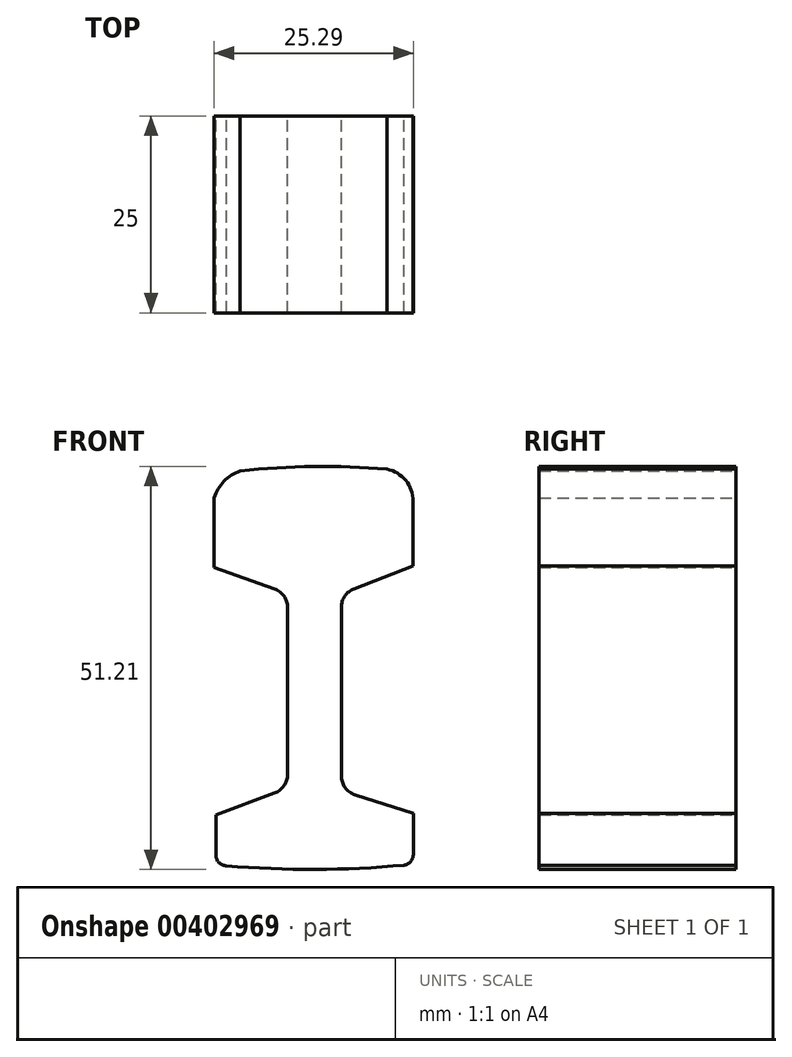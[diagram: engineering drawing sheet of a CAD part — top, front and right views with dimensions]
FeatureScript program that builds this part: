
annotation { "Feature Type Name" : "Feature", "Feature Type Description" : "" }
export const myFeature = defineFeature(function(context is Context, id is Id, definition is map)
    precondition{}
    {
        {
            var Q0;
            Q0=qCreatedBy(makeId("Front.planeOp"),FACE);
            var sketch = newSketch(context, id + "F0", { "sketchPlane" : qUnion([Q0])});
            skLineSegment(sketch, "E0", {"start": v(-32.08, 49.25) * mm, "end": v(-32.08, 28.1) * mm});
            skLineSegment(sketch, "E1", {"start": v(-25.28, 49.3) * mm, "end": v(-25.28, 27.9) * mm});
            skLineSegment(sketch, "E2", {"start": v(-23.64, 51.66) * mm, "end": v(-16.14, 54.54) * mm});
            skLineSegment(sketch, "E3", {"start": v(-33.77, 51.64) * mm, "end": v(-41.42, 54.38) * mm});
            skLineSegment(sketch, "E4", {"start": v(-33.73, 25.71) * mm, "end": v(-41.19, 22.92) * mm});
            skLineSegment(sketch, "E5", {"start": v(-23.51, 25.49) * mm, "end": v(-16.13, 23.13) * mm});
            skPoint(sketch, "E6.visualSharp", {"position": v(-32.08, 26.33) * mm});
            skArc(sketch, "E6.filletArc", {"start": v(-33.73, 25.71) * mm, "mid": v(-32.53, 26.65) * mm, "end": v(-32.08, 28.1) * mm});
            skPoint(sketch, "E7.visualSharp", {"position": v(-25.28, 26.05) * mm});
            skArc(sketch, "E7.filletArc", {"start": v(-25.28, 27.9) * mm, "mid": v(-24.79, 26.41) * mm, "end": v(-23.51, 25.49) * mm});
            skPoint(sketch, "E8.visualSharp", {"position": v(-25.28, 51.04) * mm});
            skArc(sketch, "E8.filletArc", {"start": v(-23.64, 51.66) * mm, "mid": v(-24.83, 50.73) * mm, "end": v(-25.28, 49.3) * mm});
            skPoint(sketch, "E9.visualSharp", {"position": v(-32.08, 51.04) * mm});
            skArc(sketch, "E9.filletArc", {"start": v(-32.08, 49.25) * mm, "mid": v(-32.55, 50.71) * mm, "end": v(-33.77, 51.64) * mm});
            skLineSegment(sketch, "E10", {"start": v(-16.13, 23.13) * mm, "end": v(-16.13, 17.86) * mm});
            skLineSegment(sketch, "E11", {"start": v(-41.19, 22.92) * mm, "end": v(-41.19, 17.8) * mm});
            skArc(sketch, "E12", {"start": v(-39.86, 16.47) * mm, "mid": v(-28.58, 16) * mm, "end": v(-17.3, 16.55) * mm});
            skArc(sketch, "E13", {"start": v(-41.19, 17.8) * mm, "mid": v(-40.8, 16.86) * mm, "end": v(-39.86, 16.47) * mm});
            skArc(sketch, "E14", {"start": v(-17.3, 16.55) * mm, "mid": v(-16.47, 16.98) * mm, "end": v(-16.13, 17.86) * mm});
            skLineSegment(sketch, "E15", {"start": v(-41.42, 54.38) * mm, "end": v(-41.42, 63.21) * mm});
            skLineSegment(sketch, "E16", {"start": v(-16.14, 54.54) * mm, "end": v(-16.14, 62.78) * mm});
            skArc(sketch, "E17", {"start": v(-19.49, 66.86) * mm, "mid": v(-28.8, 67.2) * mm, "end": v(-38.1, 66.62) * mm});
            skArc(sketch, "E18", {"start": v(-38.1, 66.62) * mm, "mid": v(-40.18, 65.32) * mm, "end": v(-41.42, 63.21) * mm});
            skArc(sketch, "E19", {"start": v(-16.14, 62.78) * mm, "mid": v(-17.08, 65.42) * mm, "end": v(-19.49, 66.86) * mm});
            skSolve(sketch);
        }
        {
            var Q0;
            Q0=makeQuery(id+"F0.imprint","IMPRINT",FACE,{"disambiguationData":[TD([[makeQuery(id+"F0.imprint","IMPRINT",EDGE,{"derivedFrom":sQuery(id+"F0.wireOp",EDGE,"E0")}),1.0]])]});
            extrude(context, id + "F1", {"entities" : qUnion([Q0]), "depth" : 25 * mm});
        }
    });
